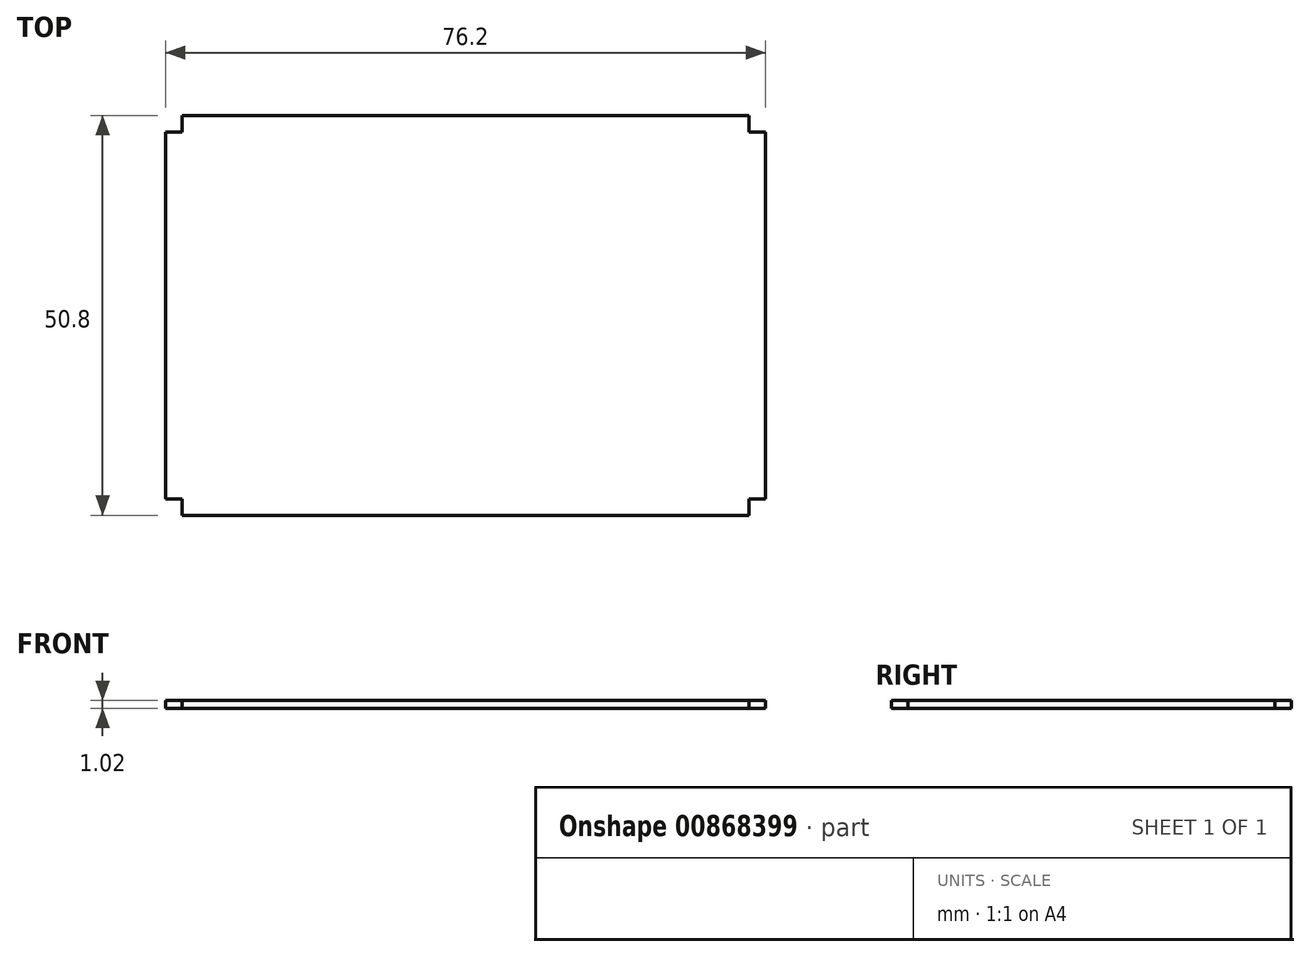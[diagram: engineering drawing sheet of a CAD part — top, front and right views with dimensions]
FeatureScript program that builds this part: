
annotation { "Feature Type Name" : "Feature", "Feature Type Description" : "" }
export const myFeature = defineFeature(function(context is Context, id is Id, definition is map)
    precondition{}
    {
        {
            var Q0;
            Q0=qCreatedBy(makeId("Top.planeOp"),FACE);
            var sketch = newSketch(context, id + "F0", { "sketchPlane" : qUnion([Q0])});
            skLineSegment(sketch, "E0.bottom", {"start": v(0, 0) * mm, "end": v(76.2, 0) * mm});
            skLineSegment(sketch, "E0.top", {"start": v(0, 50.8) * mm, "end": v(76.2, 50.8) * mm});
            skLineSegment(sketch, "E0.left", {"start": v(0, 0) * mm, "end": v(0, 50.8) * mm});
            skLineSegment(sketch, "E0.right", {"start": v(76.2, 0) * mm, "end": v(76.2, 50.8) * mm});
            skLineSegment(sketch, "E1.bottom", {"start": v(0, 50.8) * mm, "end": v(2.1, 50.8) * mm});
            skLineSegment(sketch, "E1.top", {"start": v(0, 48.7) * mm, "end": v(2.1, 48.7) * mm});
            skLineSegment(sketch, "E1.left", {"start": v(0, 50.8) * mm, "end": v(0, 48.7) * mm});
            skLineSegment(sketch, "E1.right", {"start": v(2.1, 50.8) * mm, "end": v(2.1, 48.7) * mm});
            skLineSegment(sketch, "E2.bottom", {"start": v(0, 0) * mm, "end": v(2.1, 0) * mm});
            skLineSegment(sketch, "E2.top", {"start": v(0, 2.1) * mm, "end": v(2.1, 2.1) * mm});
            skLineSegment(sketch, "E2.left", {"start": v(0, 0) * mm, "end": v(0, 2.1) * mm});
            skLineSegment(sketch, "E2.right", {"start": v(2.1, 0) * mm, "end": v(2.1, 2.1) * mm});
            skLineSegment(sketch, "E3.bottom", {"start": v(76.2, 50.8) * mm, "end": v(74.1, 50.8) * mm});
            skLineSegment(sketch, "E3.top", {"start": v(76.2, 48.7) * mm, "end": v(74.1, 48.7) * mm});
            skLineSegment(sketch, "E3.left", {"start": v(76.2, 50.8) * mm, "end": v(76.2, 48.7) * mm});
            skLineSegment(sketch, "E3.right", {"start": v(74.1, 50.8) * mm, "end": v(74.1, 48.7) * mm});
            skLineSegment(sketch, "E4.bottom", {"start": v(76.2, 0) * mm, "end": v(74.1, 0) * mm});
            skLineSegment(sketch, "E4.top", {"start": v(76.2, 2.1) * mm, "end": v(74.1, 2.1) * mm});
            skLineSegment(sketch, "E4.left", {"start": v(76.2, 0) * mm, "end": v(76.2, 2.1) * mm});
            skLineSegment(sketch, "E4.right", {"start": v(74.1, 0) * mm, "end": v(74.1, 2.1) * mm});
            skSolve(sketch);
        }
        {
            var Q0;
            {var subQ3=sQuery(id+"F0.wireOp",EDGE,"E1.top");Q0=makeQuery(id+"F0.imprint","IMPRINT",FACE,{"disambiguationData":[TD([[makeQuery(id+"F0.imprint","IMPRINT",EDGE,{"derivedFrom":subQ3}),-1.0]])]});}
            extrude(context, id + "F1", {"entities" : qUnion([Q0]), "depth" : 1.02 * mm, "offsetDistance" : 25.4 * mm});
        }
    });
